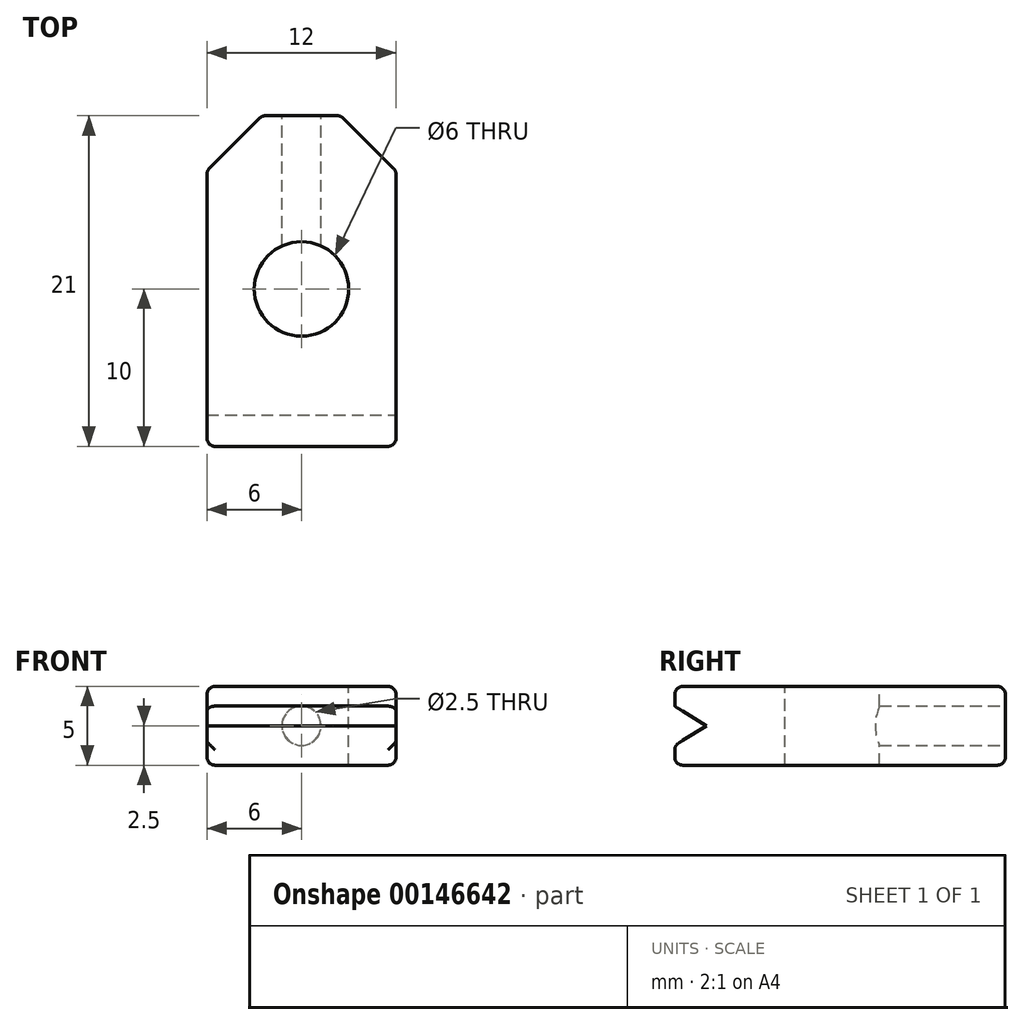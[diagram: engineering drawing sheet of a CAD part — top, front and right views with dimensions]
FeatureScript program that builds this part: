
annotation { "Feature Type Name" : "Feature", "Feature Type Description" : "" }
export const myFeature = defineFeature(function(context is Context, id is Id, definition is map)
    precondition{}
    {
        {
            var Q0;
            Q0=qCreatedBy(makeId("Top.planeOp"),FACE);
            var sketch = newSketch(context, id + "F0", { "sketchPlane" : qUnion([Q0])});
            skLineSegment(sketch, "E0", {"start": v(0, 0) * mm, "end": v(12, 0) * mm});
            skLineSegment(sketch, "E1", {"start": v(12, 0) * mm, "end": v(12, 17.5) * mm});
            skLineSegment(sketch, "E2", {"start": v(12, 17.5) * mm, "end": v(8.5, 21) * mm});
            skLineSegment(sketch, "E3", {"start": v(8.5, 21) * mm, "end": v(3.5, 21) * mm});
            skLineSegment(sketch, "E4", {"start": v(3.5, 21) * mm, "end": v(0, 17.5) * mm});
            skLineSegment(sketch, "E5", {"start": v(0, 17.5) * mm, "end": v(0, 0) * mm});
            skLineSegment(sketch, "E6", {"start": v(6, 0) * mm, "end": v(6, 31.54) * mm, "construction": true});
            skPoint(sketch, "E7", {"position": v(6, 21) * mm});
            skSolve(sketch);
        }
        {
            var Q0;
            Q0=makeQuery(id+"F0.imprint","IMPRINT",FACE,{"disambiguationData":[TD([[makeQuery(id+"F0.imprint","IMPRINT",EDGE,{"derivedFrom":sQuery(id+"F0.wireOp",EDGE,"E0")}),1.0]])]});
            extrude(context, id + "F1", {"entities" : qUnion([Q0]), "depth" : 5 * mm});
        }
        {
            var Q0;
            Q0=makeQuery(id+"F1.opExtrude","SWEPT_FACE",FACE,{"disambiguationData":[OSD([sQuery(id+"F0.wireOp",EDGE,"E1")])]});
            var sketch = newSketch(context, id + "F2", { "sketchPlane" : qUnion([Q0])});
            skLineSegment(sketch, "E8", {"start": v(0, 2.5) * mm, "end": v(17.5, 2.5) * mm, "construction": true});
            skLineSegment(sketch, "E9", {"start": v(0, 2.5) * mm, "end": v(0, 3.75) * mm});
            skLineSegment(sketch, "E10", {"start": v(0, 3.75) * mm, "end": v(2, 2.5) * mm});
            skLineSegment(sketch, "E11", {"start": v(2, 2.5) * mm, "end": v(0, 1.25) * mm});
            skLineSegment(sketch, "E12", {"start": v(0, 1.25) * mm, "end": v(0, 2.5) * mm});
            skSolve(sketch);
        }
        {
            var Q0;
            Q0=makeQuery(id+"F2.imprint","IMPRINT",FACE,{"disambiguationData":[TD([[makeQuery(id+"F2.imprint","IMPRINT",EDGE,{"derivedFrom":sQuery(id+"F2.wireOp",EDGE,"E9")}),1.0]])]});
            extrude(context, id + "F3", {"entities" : qUnion([Q0]), "operationType" : NewBodyOperationType.REMOVE, "endBound" : BoundingType.THROUGH_ALL, "oppositeDirection" : true, "depth" : 25 * mm});
        }
        {
            var Q0;
            Q0=makeQuery(id+"F1.opExtrude","CAP_FACE",FACE,{"disambiguationData":[OSD([sQuery(id+"F0.wireOp",EDGE,"E0"),sQuery(id+"F0.wireOp",EDGE,"E1"),sQuery(id+"F0.wireOp",EDGE,"E2"),sQuery(id+"F0.wireOp",EDGE,"E3"),sQuery(id+"F0.wireOp",EDGE,"E4"),sQuery(id+"F0.wireOp",EDGE,"E5")])],"isStart":false});
            var sketch = newSketch(context, id + "F4", { "sketchPlane" : qUnion([Q0])});
            skLineSegment(sketch, "E13", {"start": v(6, 0) * mm, "end": v(6, 10) * mm});
            skCircle(sketch, "E14", {"center": v(6, 10) * mm, "radius": 3 * mm});
            skSolve(sketch);
        }
        {
            var Q0;
            Q0=makeQuery(id+"F4.imprint","IMPRINT",FACE,{"disambiguationData":[TD([[makeQuery(id+"F4.imprint","IMPRINT",EDGE,{"derivedFrom":sQuery(id+"F4.wireOp",EDGE,"E14")}),1.0]])]});
            extrude(context, id + "F5", {"entities" : qUnion([Q0]), "operationType" : NewBodyOperationType.REMOVE, "endBound" : BoundingType.THROUGH_ALL, "oppositeDirection" : true, "depth" : 25 * mm});
        }
        {
            var Q0;
            Q0=makeQuery(id+"F1.opExtrude","SWEPT_FACE",FACE,{"disambiguationData":[OSD([sQuery(id+"F0.wireOp",EDGE,"E3")])]});
            var sketch = newSketch(context, id + "F6", { "sketchPlane" : qUnion([Q0])});
            skPoint(sketch, "E15.centerSnap0", {"position": v(-6, 0) * mm});
            skPoint(sketch, "E15.centerSnap1", {"position": v(-8.5, 2.5) * mm});
            skPoint(sketch, "E16", {"position": v(-6, 2.5) * mm});
            skSolve(sketch);
        }
        {
            var Q0;
            Q0=sQuery(id+"F6.wireOp",VERTEX,"E16");
            var Q1;
            Q1=makeQuery(id+"F1.opExtrude","SWEPT_BODY",BODY,{"disambiguationData":[OSD([sQuery(id+"F0.wireOp",EDGE,"E0"),sQuery(id+"F0.wireOp",EDGE,"E1"),sQuery(id+"F0.wireOp",EDGE,"E2"),sQuery(id+"F0.wireOp",EDGE,"E3"),sQuery(id+"F0.wireOp",EDGE,"E4"),sQuery(id+"F0.wireOp",EDGE,"E5")])]});
            hole(context, id + "F7", {"style" : HoleStyle.SIMPLE, "endStyle" : HoleEndStyle.BLIND, "standardTappedOrClearance" : lookupTablePath({ "standard" : "ISO", "engagement" : "75%", "pitch" : "0.5 mm", "size" : "M3", "type" : "Tapped" }), "standardBlindInLast" : lookupTablePath({ "standard" : "ISO", "engagement" : "75%", "pitch" : "0.5 mm", "size" : "M3", "type" : "Tapped" }), "holeDiameter" : 2.5 * mm, "holeDepth" : 12 * mm, "locations" : qUnion([Q0]), "scope" : qUnion([Q1]), "majorDiameter" : 3 * mm});
        }
        {
            var Q0;
            Q0=makeQuery(id+"F1.opExtrude","CAP_EDGE",EDGE,{"disambiguationData":[OSD([sQuery(id+"F0.wireOp",EDGE,"E4")])],"isStart":false});
            var Q1;
            Q1=makeQuery(id+"F1.opExtrude","SWEPT_EDGE",EDGE,{"disambiguationData":[OSD([sQuery(id+"F0.wireOp",EDGE,"E3"),sQuery(id+"F0.wireOp",EDGE,"E4")])]});
            var Q2;
            Q2=makeQuery(id+"F1.opExtrude","CAP_EDGE",EDGE,{"disambiguationData":[OSD([sQuery(id+"F0.wireOp",EDGE,"E4")])],"isStart":true});
            var Q3;
            Q3=makeQuery(id+"F1.opExtrude","CAP_EDGE",EDGE,{"disambiguationData":[OSD([sQuery(id+"F0.wireOp",EDGE,"E3")])],"isStart":false});
            var Q4;
            Q4=makeQuery(id+"F1.opExtrude","SWEPT_EDGE",EDGE,{"disambiguationData":[OSD([sQuery(id+"F0.wireOp",EDGE,"E2"),sQuery(id+"F0.wireOp",EDGE,"E3")])]});
            var Q5;
            Q5=makeQuery(id+"F1.opExtrude","CAP_EDGE",EDGE,{"disambiguationData":[OSD([sQuery(id+"F0.wireOp",EDGE,"E3")])],"isStart":true});
            var Q6;
            Q6=makeQuery(id+"F1.opExtrude","CAP_EDGE",EDGE,{"disambiguationData":[OSD([sQuery(id+"F0.wireOp",EDGE,"E2")])],"isStart":true});
            var Q7;
            Q7=makeQuery(id+"F1.opExtrude","CAP_EDGE",EDGE,{"disambiguationData":[OSD([sQuery(id+"F0.wireOp",EDGE,"E2")])],"isStart":false});
            var Q8;
            Q8=makeQuery(id+"F1.opExtrude","SWEPT_EDGE",EDGE,{"disambiguationData":[OSD([sQuery(id+"F0.wireOp",EDGE,"E1"),sQuery(id+"F0.wireOp",EDGE,"E2")])]});
            var Q9;
            Q9=makeQuery(id+"F1.opExtrude","SWEPT_EDGE",EDGE,{"disambiguationData":[OSD([sQuery(id+"F0.wireOp",EDGE,"E4"),sQuery(id+"F0.wireOp",EDGE,"E5")])]});
            var Q10;
            Q10=makeQuery(id+"F1.opExtrude","CAP_EDGE",EDGE,{"disambiguationData":[OSD([sQuery(id+"F0.wireOp",EDGE,"E5")])],"isStart":false});
            var Q11;
            Q11=makeQuery(id+"F1.opExtrude","CAP_EDGE",EDGE,{"disambiguationData":[OSD([sQuery(id+"F0.wireOp",EDGE,"E5")])],"isStart":true});
            var Q12;
            Q12=makeQuery(id+"F1.opExtrude","CAP_EDGE",EDGE,{"disambiguationData":[OSD([sQuery(id+"F0.wireOp",EDGE,"E1")])],"isStart":false});
            var Q13;
            Q13=makeQuery(id+"F1.opExtrude","CAP_EDGE",EDGE,{"disambiguationData":[OSD([sQuery(id+"F0.wireOp",EDGE,"E1")])],"isStart":true});
            var Q14;
            {var subQ0=sQuery(id+"F0.wireOp",EDGE,"E0");var subQ1=sQuery(id+"F0.wireOp",EDGE,"E1");Q14=makeQuery(id+"F3.boolean.opBoolean","SPLIT",EDGE,{"disambiguationData":[TD([makeQuery(id+"F3.opExtrude","SWEPT_FACE",FACE,{"disambiguationData":[OSD([sQuery(id+"F2.wireOp",EDGE,"E11")])]})])],"derivedFrom":makeQuery(id+"F1.opExtrude","SWEPT_EDGE",EDGE,{"disambiguationData":[OSD([subQ0,subQ1])]})});}
            var Q15;
            Q15=makeQuery(id+"F3.boolean.opBoolean","COPY",EDGE,{"derivedFrom":makeQuery(id+"F3.opExtrude","SWEPT_EDGE",EDGE,{"disambiguationData":[OSD([sQuery(id+"F0.wireOp",EDGE,"E0"),sQuery(id+"F0.wireOp",EDGE,"E1"),sQuery(id+"F2.wireOp",EDGE,"E11"),sQuery(id+"F2.wireOp",EDGE,"E12")])]})});
            var Q16;
            Q16=makeQuery(id+"F1.opExtrude","CAP_EDGE",EDGE,{"disambiguationData":[OSD([sQuery(id+"F0.wireOp",EDGE,"E0")])],"isStart":true});
            var Q17;
            {var subQ0=sQuery(id+"F0.wireOp",EDGE,"E0");var subQ1=sQuery(id+"F0.wireOp",EDGE,"E1");Q17=makeQuery(id+"F3.boolean.opBoolean","SPLIT",EDGE,{"disambiguationData":[TD([makeQuery(id+"F3.opExtrude","SWEPT_FACE",FACE,{"disambiguationData":[OSD([sQuery(id+"F2.wireOp",EDGE,"E10")])]})])],"derivedFrom":makeQuery(id+"F1.opExtrude","SWEPT_EDGE",EDGE,{"disambiguationData":[OSD([subQ0,subQ1])]})});}
            var Q18;
            Q18=makeQuery(id+"F3.boolean.opBoolean","COPY",EDGE,{"derivedFrom":makeQuery(id+"F3.opExtrude","SWEPT_EDGE",EDGE,{"disambiguationData":[OSD([sQuery(id+"F0.wireOp",EDGE,"E0"),sQuery(id+"F0.wireOp",EDGE,"E1"),sQuery(id+"F2.wireOp",EDGE,"E9"),sQuery(id+"F2.wireOp",EDGE,"E10")])]})});
            var Q19;
            Q19=makeQuery(id+"F1.opExtrude","CAP_EDGE",EDGE,{"disambiguationData":[OSD([sQuery(id+"F0.wireOp",EDGE,"E0")])],"isStart":false});
            var Q20;
            {var subQ0=sQuery(id+"F0.wireOp",EDGE,"E0");var subQ1=sQuery(id+"F0.wireOp",EDGE,"E5");Q20=makeQuery(id+"F3.boolean.opBoolean","SPLIT",EDGE,{"disambiguationData":[TD([makeQuery(id+"F3.opExtrude","SWEPT_FACE",FACE,{"disambiguationData":[OSD([sQuery(id+"F2.wireOp",EDGE,"E10")])]})])],"derivedFrom":makeQuery(id+"F1.opExtrude","SWEPT_EDGE",EDGE,{"disambiguationData":[OSD([subQ0,subQ1])]})});}
            var Q21;
            {var subQ0=sQuery(id+"F0.wireOp",EDGE,"E0");var subQ1=sQuery(id+"F0.wireOp",EDGE,"E5");Q21=makeQuery(id+"F3.boolean.opBoolean","SPLIT",EDGE,{"disambiguationData":[TD([makeQuery(id+"F3.opExtrude","SWEPT_FACE",FACE,{"disambiguationData":[OSD([sQuery(id+"F2.wireOp",EDGE,"E11")])]})])],"derivedFrom":makeQuery(id+"F1.opExtrude","SWEPT_EDGE",EDGE,{"disambiguationData":[OSD([subQ0,subQ1])]})});}
            fillet(context, id + "F8", {"entities" : qUnion([Q0, Q1, Q2, Q3, Q4, Q5, Q6, Q7, Q8, Q9, Q10, Q11, Q12, Q13, Q14, Q15, Q16, Q17, Q18, Q19, Q20, Q21]), "radius" : 0.5 * mm, "tangentPropagation" : true, "allowEdgeOverflow" : false});
        }
    });
